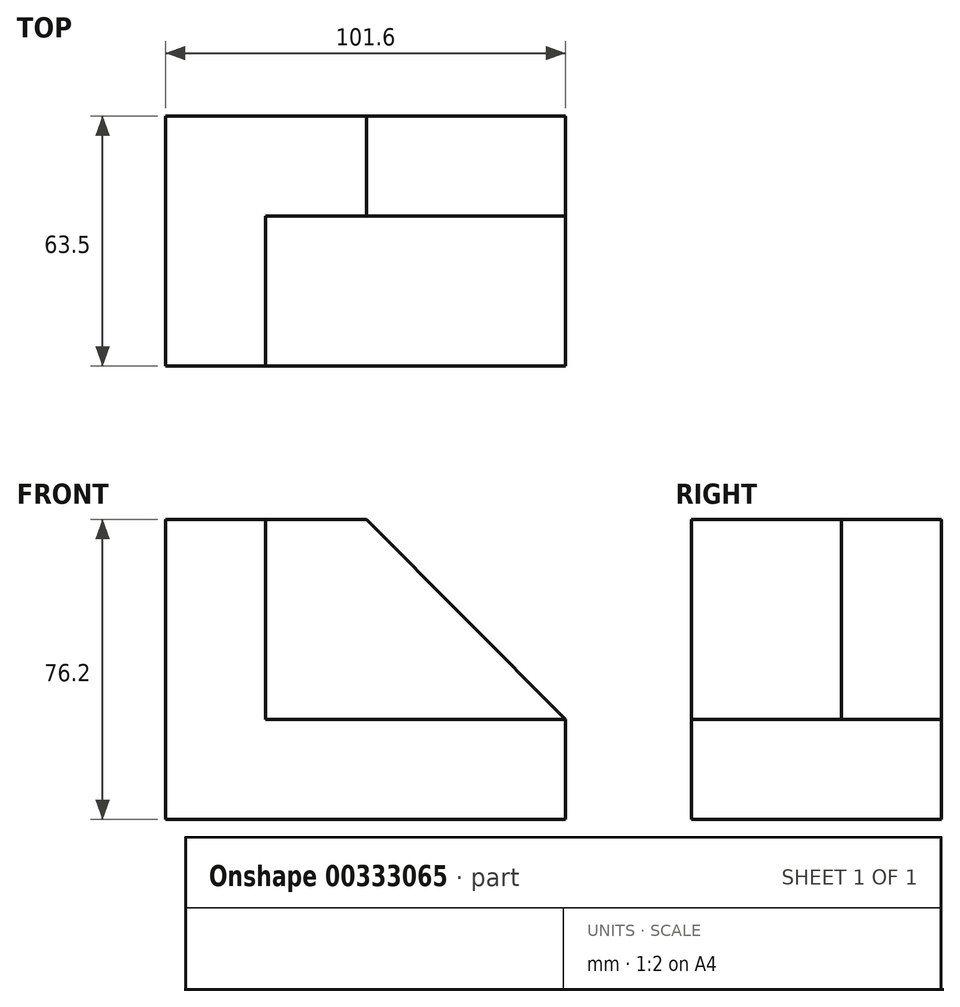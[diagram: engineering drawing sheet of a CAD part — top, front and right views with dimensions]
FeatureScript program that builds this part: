
annotation { "Feature Type Name" : "Feature", "Feature Type Description" : "" }
export const myFeature = defineFeature(function(context is Context, id is Id, definition is map)
    precondition{}
    {
        {
            var Q0;
            Q0=qCreatedBy(makeId("Front.planeOp"),FACE);
            var sketch = newSketch(context, id + "F0", { "sketchPlane" : qUnion([Q0])});
            skLineSegment(sketch, "E0", {"start": v(-51.1, 16.1) * mm, "end": v(50.5, 16.1) * mm});
            skLineSegment(sketch, "E1", {"start": v(50.5, 16.1) * mm, "end": v(50.5, -9.3) * mm});
            skLineSegment(sketch, "E2", {"start": v(50.5, -9.3) * mm, "end": v(-51.1, -9.3) * mm});
            skLineSegment(sketch, "E3", {"start": v(-51.1, -9.3) * mm, "end": v(-51.1, 16.1) * mm});
            skSolve(sketch);
        }
        {
            var Q0;
            Q0=makeQuery(id+"F0.imprint","IMPRINT",FACE,{"disambiguationData":[TD([[makeQuery(id+"F0.imprint","IMPRINT",EDGE,{"derivedFrom":sQuery(id+"F0.wireOp",EDGE,"E0")}),-1.0]])]});
            extrude(context, id + "F1", {"entities" : qUnion([Q0]), "depth" : 63.5 * mm});
        }
        {
            var Q0;
            Q0=makeQuery(id+"F1.opExtrude","SWEPT_FACE",FACE,{"disambiguationData":[OSD([sQuery(id+"F0.wireOp",EDGE,"E0")])]});
            var sketch = newSketch(context, id + "F2", { "sketchPlane" : qUnion([Q0])});
            skLineSegment(sketch, "E4", {"start": v(-51.1, 0) * mm, "end": v(-25.7, 0) * mm});
            skLineSegment(sketch, "E5", {"start": v(-25.7, 0) * mm, "end": v(-25.7, -63.5) * mm});
            skLineSegment(sketch, "E6", {"start": v(-25.7, -63.5) * mm, "end": v(-51.1, -63.5) * mm});
            skLineSegment(sketch, "E7", {"start": v(-51.1, -63.5) * mm, "end": v(-51.1, 0) * mm});
            skSolve(sketch);
        }
        {
            var Q0;
            Q0=makeQuery(id+"F2.imprint","IMPRINT",FACE,{"disambiguationData":[TD([[makeQuery(id+"F2.imprint","IMPRINT",EDGE,{"derivedFrom":sQuery(id+"F2.wireOp",EDGE,"E4")}),-1.0]])]});
            extrude(context, id + "F3", {"entities" : qUnion([Q0]), "operationType" : NewBodyOperationType.ADD, "depth" : 50.8 * mm});
        }
        {
            var Q0;
            Q0=makeQuery(id+"F1.opExtrude","SWEPT_FACE",FACE,{"disambiguationData":[OSD([sQuery(id+"F0.wireOp",EDGE,"E0")])]});
            var sketch = newSketch(context, id + "F4", { "sketchPlane" : qUnion([Q0])});
            skLineSegment(sketch, "E8", {"start": v(-25.7, 0) * mm, "end": v(0, 0) * mm});
            skLineSegment(sketch, "E9", {"start": v(0, 0) * mm, "end": v(0, -25.4) * mm});
            skLineSegment(sketch, "E10", {"start": v(0, -25.4) * mm, "end": v(-25.7, -25.4) * mm});
            skLineSegment(sketch, "E11", {"start": v(-25.7, -25.4) * mm, "end": v(-25.7, 0) * mm});
            skSolve(sketch);
        }
        {
            var Q0;
            Q0=makeQuery(id+"F4.imprint","IMPRINT",FACE,{"disambiguationData":[TD([[makeQuery(id+"F4.imprint","IMPRINT",EDGE,{"derivedFrom":sQuery(id+"F4.wireOp",EDGE,"E8")}),-1.0]])]});
            extrude(context, id + "F5", {"entities" : qUnion([Q0]), "operationType" : NewBodyOperationType.ADD, "depth" : 50.8 * mm});
        }
        {
            var Q0;
            Q0=makeQuery(id+"F5.opExtrude","SWEPT_FACE",FACE,{"disambiguationData":[OSD([sQuery(id+"F4.wireOp",EDGE,"E10")])]});
            var sketch = newSketch(context, id + "F6", { "sketchPlane" : qUnion([Q0])});
            skLineSegment(sketch, "E12", {"start": v(0, 66.9) * mm, "end": v(50.45, 16.1) * mm});
            skPoint(sketch, "E13.endSnap0", {"position": v(25.23, 41.5) * mm});
            skLineSegment(sketch, "E14", {"start": v(50.45, 16.1) * mm, "end": v(0, 16.1) * mm});
            skLineSegment(sketch, "E15", {"start": v(0, 16.1) * mm, "end": v(0, 66.9) * mm});
            skSolve(sketch);
        }
        {
            var Q0;
            Q0=makeQuery(id+"F6.imprint","IMPRINT",FACE,{"disambiguationData":[TD([[makeQuery(id+"F6.imprint","IMPRINT",EDGE,{"derivedFrom":sQuery(id+"F6.wireOp",EDGE,"E12")}),-1.0]])]});
            extrude(context, id + "F7", {"entities" : qUnion([Q0]), "operationType" : NewBodyOperationType.ADD, "oppositeDirection" : true, "depth" : 25.4 * mm});
        }
    });
